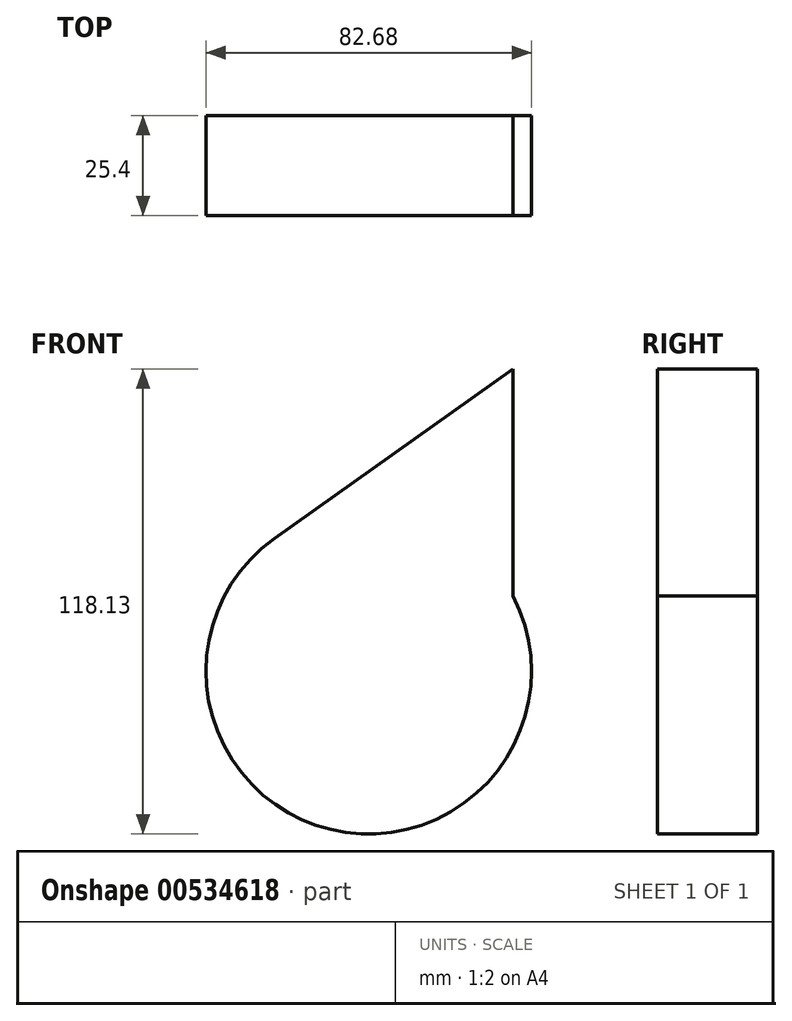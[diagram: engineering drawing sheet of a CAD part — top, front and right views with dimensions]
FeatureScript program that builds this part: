
annotation { "Feature Type Name" : "Feature", "Feature Type Description" : "" }
export const myFeature = defineFeature(function(context is Context, id is Id, definition is map)
    precondition{}
    {
        {
            var Q0;
            Q0=qCreatedBy(makeId("Front.planeOp"),FACE);
            var sketch = newSketch(context, id + "F0", { "sketchPlane" : qUnion([Q0])});
            skCircle(sketch, "E0", {"center": v(0, 0) * mm, "radius": 41.34 * mm});
            skArc(sketch, "E1", {"start": v(36.63, 19.17) * mm, "mid": v(26.23, -0.02) * mm, "end": v(36.59, -19.24) * mm});
            skLineSegment(sketch, "E2", {"start": v(36.63, 19.17) * mm, "end": v(36.63, 76.8) * mm});
            skLineSegment(sketch, "E3", {"start": v(36.63, 76.8) * mm, "end": v(-23.97, 33.68) * mm});
            skSolve(sketch);
        }
        {
            var Q0;
            Q0=qCreatedBy(makeId("Front.planeOp"),FACE);
            var sketch = newSketch(context, id + "F1", { "sketchPlane" : qUnion([Q0])});
            skSolve(sketch);
        }
        {
            var Q0;
            Q0 = qSketchRegion(id + "F1", true);
            var Q1;
            {var subQ0=sQuery(id+"F0.wireOp",EDGE,"E1");Q1=makeQuery(id+"F0.imprint","IMPRINT",FACE,{"disambiguationData":[TD([[makeQuery(id+"F0.imprint","IMPRINT",EDGE,{"derivedFrom":subQ0}),-1.0]])]});}
            extrude(context, id + "F2", {"entities" : qUnion([Q0, Q1]), "depth" : 25.4 * mm, "offsetDistance" : 25.4 * mm});
        }
        {
            var Q0;
            Q0 = qSketchRegion(id + "F0", true);
            extrude(context, id + "F3", {"entities" : qUnion([Q0]), "operationType" : NewBodyOperationType.ADD, "depth" : 25.4 * mm, "offsetDistance" : 25.4 * mm});
        }
    });
